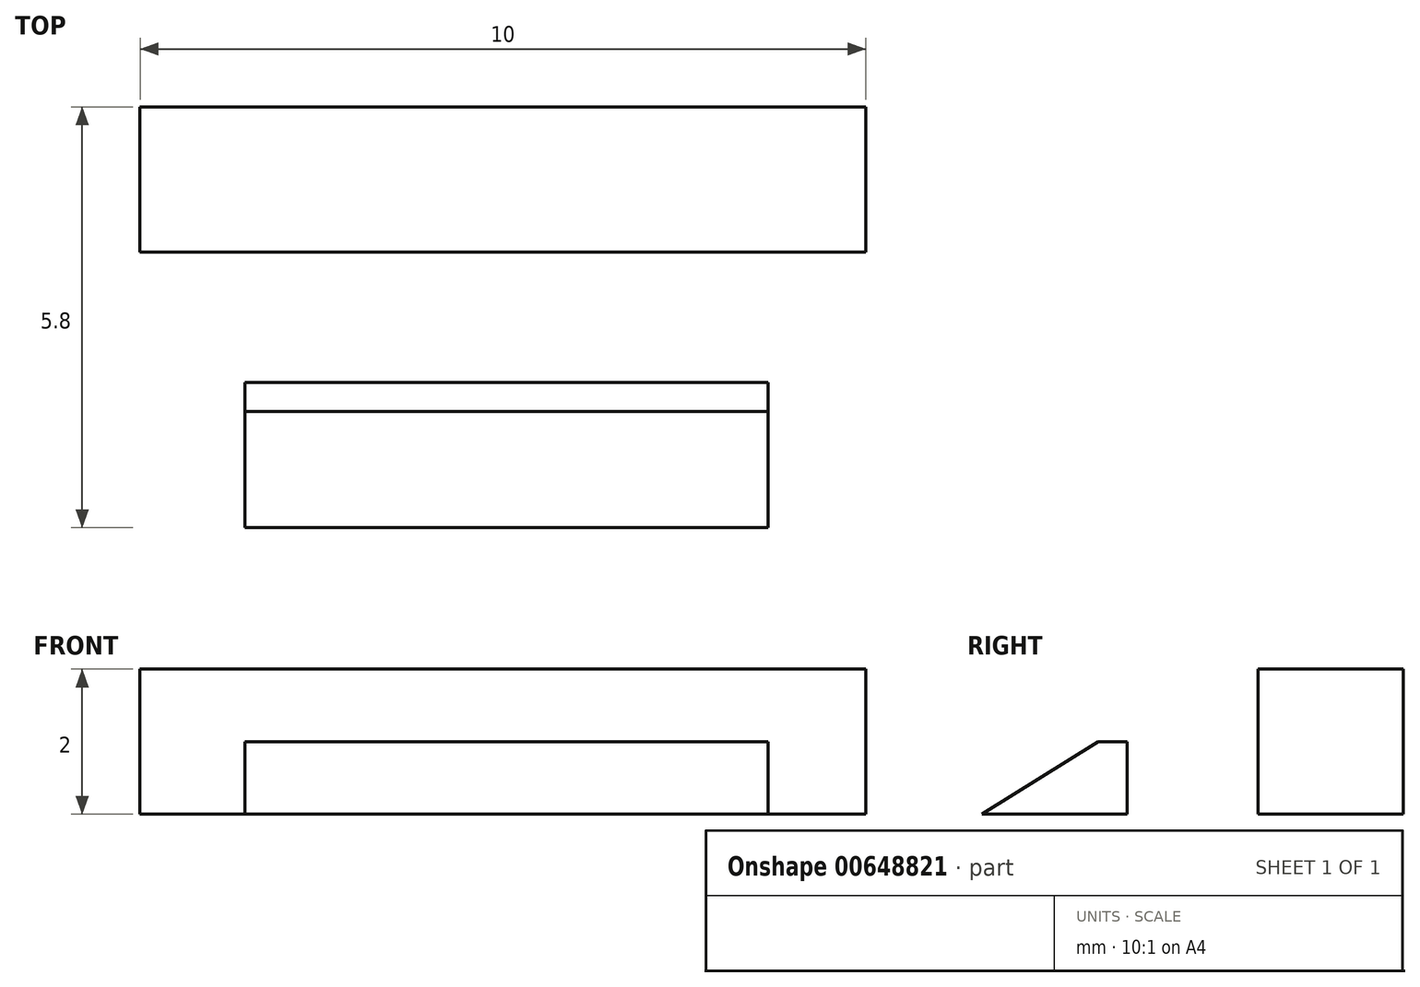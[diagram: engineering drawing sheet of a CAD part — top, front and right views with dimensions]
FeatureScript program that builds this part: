
annotation { "Feature Type Name" : "Feature", "Feature Type Description" : "" }
export const myFeature = defineFeature(function(context is Context, id is Id, definition is map)
    precondition{}
    {
        {
            var Q0;
            Q0=qCreatedBy(makeId("Top.planeOp"),FACE);
            var sketch = newSketch(context, id + "F0", { "sketchPlane" : qUnion([Q0])});
            skLineSegment(sketch, "E0.bottom", {"start": v(-23.56, 2) * mm, "end": v(-13.56, 2) * mm});
            skLineSegment(sketch, "E0.top", {"start": v(-23.56, 0) * mm, "end": v(-13.56, 0) * mm});
            skLineSegment(sketch, "E0.left", {"start": v(-23.56, 2) * mm, "end": v(-23.56, 0) * mm});
            skLineSegment(sketch, "E0.right", {"start": v(-13.56, 2) * mm, "end": v(-13.56, 0) * mm});
            skLineSegment(sketch, "E1.bottom", {"start": v(-21.7, 0) * mm, "end": v(-15.37, 0) * mm});
            skLineSegment(sketch, "E1.top", {"start": v(-21.7, -2) * mm, "end": v(-15.37, -2) * mm});
            skLineSegment(sketch, "E1.left", {"start": v(-21.7, 0) * mm, "end": v(-21.7, -2) * mm});
            skLineSegment(sketch, "E1.right", {"start": v(-15.37, 0) * mm, "end": v(-15.37, -2) * mm});
            skSolve(sketch);
        }
        {
            var Q0;
            Q0=makeQuery(id+"F0.imprint","IMPRINT",FACE,{"disambiguationData":[TD([[makeQuery(id+"F0.imprint","IMPRINT",EDGE,{"derivedFrom":sQuery(id+"F0.wireOp",EDGE,"E0.bottom")}),-1.0]])]});
            var Q1;
            Q1=makeQuery(id+"F0.imprint","IMPRINT",FACE,{"disambiguationData":[TD([[makeQuery(id+"F0.imprint","IMPRINT",EDGE,{"derivedFrom":sQuery(id+"F0.wireOp",EDGE,"E1.bottom")}),-1.0]])]});
            extrude(context, id + "F1", {"entities" : qUnion([Q0, Q1]), "depth" : 1 * mm, "offsetDistance" : 25 * mm});
        }
        {
            var Q0;
            Q0=makeQuery(id+"F0.imprint","IMPRINT",FACE,{"disambiguationData":[TD([[makeQuery(id+"F0.imprint","IMPRINT",EDGE,{"derivedFrom":sQuery(id+"F0.wireOp",EDGE,"E0.bottom")}),-1.0]])]});
            extrude(context, id + "F2", {"entities" : qUnion([Q0]), "operationType" : NewBodyOperationType.ADD, "oppositeDirection" : true, "depth" : 1 * mm, "offsetDistance" : 25 * mm});
        }
        {
            var Q0;
            Q0=makeQuery(id+"F2.opExtrude","CAP_FACE",FACE,{"disambiguationData":[OSD([sQuery(id+"F0.wireOp",EDGE,"E0.bottom"),sQuery(id+"F0.wireOp",EDGE,"E0.top"),sQuery(id+"F0.wireOp",EDGE,"E0.left"),sQuery(id+"F0.wireOp",EDGE,"E0.right"),sQuery(id+"F0.wireOp",EDGE,"E1.bottom")])],"isStart":false});
            var sketch = newSketch(context, id + "F3", { "sketchPlane" : qUnion([Q0])});
            skLineSegment(sketch, "E2.bottom", {"start": v(-22.11, 1.8) * mm, "end": v(-14.9, 1.8) * mm});
            skLineSegment(sketch, "E2.top", {"start": v(-22.11, 3.8) * mm, "end": v(-14.9, 3.8) * mm});
            skLineSegment(sketch, "E2.left", {"start": v(-22.11, 1.8) * mm, "end": v(-22.11, 3.8) * mm});
            skLineSegment(sketch, "E2.right", {"start": v(-14.9, 1.8) * mm, "end": v(-14.9, 3.8) * mm});
            skSolve(sketch);
        }
        {
            var Q0;
            Q0=makeQuery(id+"F3.imprint","IMPRINT",FACE,{"disambiguationData":[TD([[makeQuery(id+"F3.imprint","IMPRINT",EDGE,{"derivedFrom":sQuery(id+"F3.wireOp",EDGE,"E2.bottom")}),1.0]])]});
            extrude(context, id + "F4", {"entities" : qUnion([Q0]), "operationType" : NewBodyOperationType.ADD, "oppositeDirection" : true, "depth" : 1 * mm, "offsetDistance" : 25 * mm});
        }
        {
            var Q0;
            Q0=makeQuery(id+"F4.opExtrude","CAP_EDGE",EDGE,{"disambiguationData":[OSD([sQuery(id+"F3.wireOp",EDGE,"E2.top")])],"isStart":false});
            chamfer(context, id + "F5", {"entities" : qUnion([Q0]), "chamferType" : ChamferType.TWO_OFFSETS, "width1" : 1.6 * mm, "oppositeDirection" : false, "width2" : 1 * mm, "tangentPropagation" : true});
        }
    });
